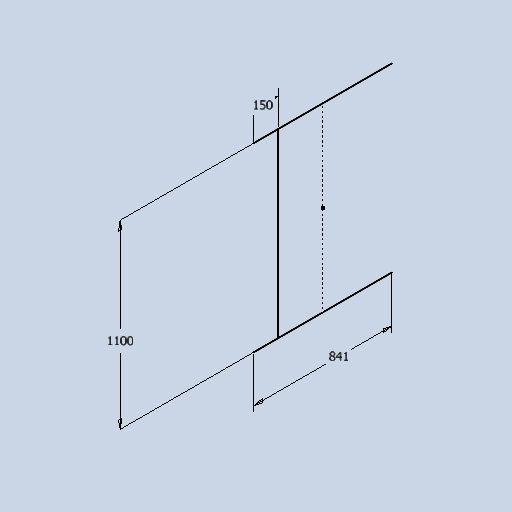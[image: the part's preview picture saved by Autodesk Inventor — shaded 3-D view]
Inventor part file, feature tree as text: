
AUTODESK INVENTOR PART (.ipt)
format: ipt  version: 2025 (Build 290162010, 162A)  size: 251,904 bytes
history: native  units: mm
features: sketch x1
ambient origin geometry x8: Origin, YZ Plane, XZ Plane, XY Plane, X Axis, Y Axis, Z Axis, Center Point
feature tree (1):
  sketch  "Sketch1"  dims[d0=1100.0mm d1=841.0mm d2=150.0mm]
